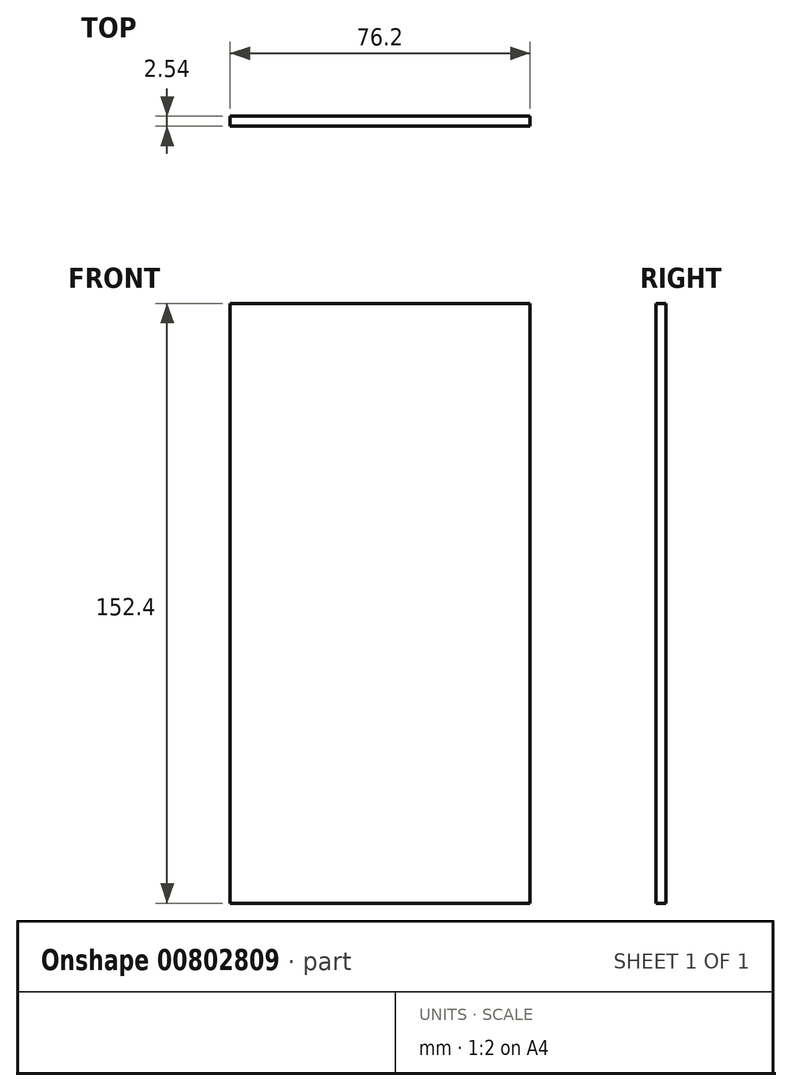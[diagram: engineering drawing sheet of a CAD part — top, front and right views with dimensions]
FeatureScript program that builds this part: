
annotation { "Feature Type Name" : "Feature", "Feature Type Description" : "" }
export const myFeature = defineFeature(function(context is Context, id is Id, definition is map)
    precondition{}
    {
        {
            var Q0;
            Q0=qCreatedBy(makeId("Front.planeOp"),FACE);
            var sketch = newSketch(context, id + "F0", { "sketchPlane" : qUnion([Q0])});
            skLineSegment(sketch, "E0.bottom", {"start": v(0, 0) * mm, "end": v(-76.2, 0) * mm});
            skLineSegment(sketch, "E0.top", {"start": v(0, 152.4) * mm, "end": v(-76.2, 152.4) * mm});
            skLineSegment(sketch, "E0.left", {"start": v(0, 0) * mm, "end": v(0, 152.4) * mm});
            skLineSegment(sketch, "E0.right", {"start": v(-76.2, 0) * mm, "end": v(-76.2, 152.4) * mm});
            skSolve(sketch);
        }
        {
            var Q0;
            Q0=makeQuery(id+"F0.imprint","IMPRINT",FACE,{"disambiguationData":[TD([[makeQuery(id+"F0.imprint","IMPRINT",EDGE,{"derivedFrom":sQuery(id+"F0.wireOp",EDGE,"E0.bottom")}),-1.0]])]});
            extrude(context, id + "F1", {"entities" : qUnion([Q0]), "depth" : 2.54 * mm, "offsetDistance" : 25.4 * mm});
        }
    });
